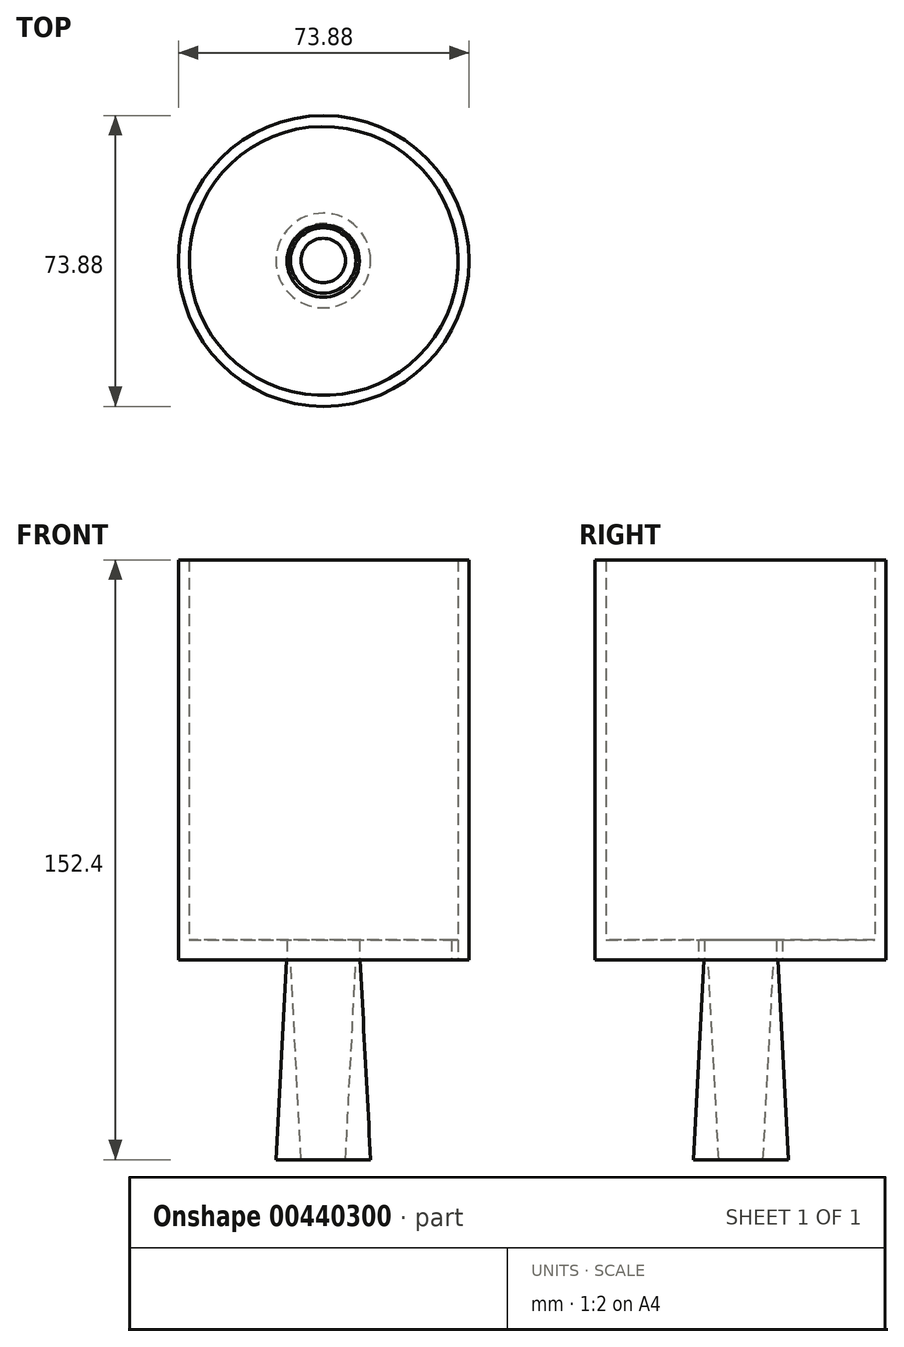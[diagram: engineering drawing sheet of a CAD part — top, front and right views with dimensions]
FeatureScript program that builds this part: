
annotation { "Feature Type Name" : "Feature", "Feature Type Description" : "" }
export const myFeature = defineFeature(function(context is Context, id is Id, definition is map)
    precondition{}
    {
        {
            var Q0;
            Q0=qCreatedBy(makeId("Top.planeOp"),FACE);
            var sketch = newSketch(context, id + "F0", { "sketchPlane" : qUnion([Q0])});
            skCircle(sketch, "E0", {"center": v(0, 22.48) * mm, "radius": 36.94 * mm});
            skCircle(sketch, "E1", {"center": v(0, 22.48) * mm, "radius": 34.15 * mm});
            skSolve(sketch);
        }
        {
            var Q0;
            Q0=makeQuery(id+"F0.imprint","IMPRINT",FACE,{"disambiguationData":[TD([[makeQuery(id+"F0.imprint","IMPRINT",EDGE,{"derivedFrom":sQuery(id+"F0.wireOp",EDGE,"E0")}),1.0]])]});
            extrude(context, id + "F1", {"entities" : qUnion([Q0]), "depth" : 101.6 * mm});
        }
        {
            var Q0;
            Q0=makeQuery(id+"F0.imprint","IMPRINT",FACE,{"disambiguationData":[TD([[makeQuery(id+"F0.imprint","IMPRINT",EDGE,{"derivedFrom":sQuery(id+"F0.wireOp",EDGE,"E1")}),1.0]])]});
            var sketch = newSketch(context, id + "F2", { "sketchPlane" : qUnion([Q0])});
            skCircle(sketch, "E2", {"center": v(-0.12, 22.48) * mm, "radius": 34.26 * mm});
            skCircle(sketch, "E3", {"center": v(-0.12, 22.48) * mm, "radius": 9.19 * mm});
            skSolve(sketch);
        }
        {
            var Q0;
            Q0=makeQuery(id+"F2.imprint","IMPRINT",FACE,{"disambiguationData":[TD([[makeQuery(id+"F2.imprint","IMPRINT",EDGE,{"derivedFrom":sQuery(id+"F2.wireOp",EDGE,"E3")}),-1.0]])]});
            extrude(context, id + "F3", {"entities" : qUnion([Q0]), "operationType" : NewBodyOperationType.ADD, "depth" : 5.08 * mm});
        }
        {
            var Q0;
            Q0=qCreatedBy(makeId("Top.planeOp"),FACE);
            var sketch = newSketch(context, id + "F4", { "sketchPlane" : qUnion([Q0])});
            skCircle(sketch, "E4", {"center": v(-0.12, 22.6) * mm, "radius": 9.36 * mm});
            skCircle(sketch, "E5", {"center": v(-0.12, 22.6) * mm, "radius": 8.3 * mm});
            skSolve(sketch);
        }
        {
            var Q0;
            Q0 = qSketchRegion(id + "F4", true);
            extrude(context, id + "F5", {"entities" : qUnion([Q0]), "operationType" : NewBodyOperationType.ADD, "oppositeDirection" : true, "depth" : 50.8 * mm, "hasDraft" : true, "draftAngle" : 3 * degree});
        }
    });
